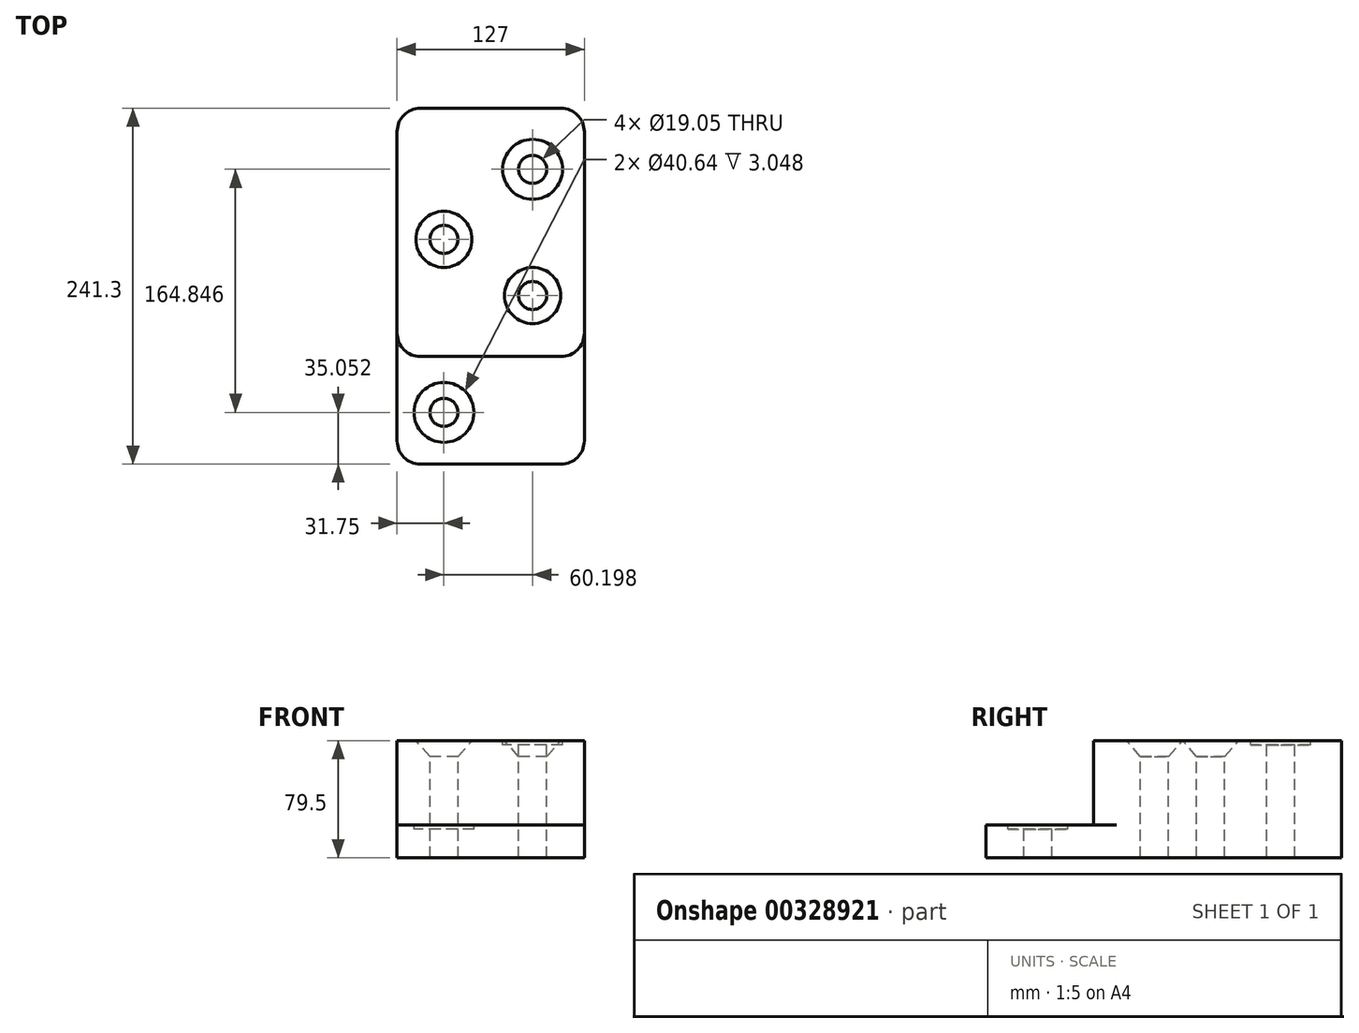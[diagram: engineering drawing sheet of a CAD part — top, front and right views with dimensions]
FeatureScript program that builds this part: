
annotation { "Feature Type Name" : "Feature", "Feature Type Description" : "" }
export const myFeature = defineFeature(function(context is Context, id is Id, definition is map)
    precondition{}
    {
        {
            var Q0;
            Q0=qCreatedBy(makeId("Top.planeOp"),FACE);
            var sketch = newSketch(context, id + "F0", { "sketchPlane" : qUnion([Q0])});
            skLineSegment(sketch, "E0.bottom", {"start": v(0, 0) * mm, "end": v(-127, 0) * mm});
            skLineSegment(sketch, "E0.top", {"start": v(0, -241.3) * mm, "end": v(-127, -241.3) * mm});
            skLineSegment(sketch, "E0.left", {"start": v(0, 0) * mm, "end": v(0, -241.3) * mm});
            skLineSegment(sketch, "E0.right", {"start": v(-127, 0) * mm, "end": v(-127, -241.3) * mm});
            skSolve(sketch);
        }
        {
            var Q0;
            Q0=makeQuery(id+"F0.imprint","IMPRINT",FACE,{"disambiguationData":[TD([[makeQuery(id+"F0.imprint","IMPRINT",EDGE,{"derivedFrom":sQuery(id+"F0.wireOp",EDGE,"E0.bottom")}),1.0]])]});
            extrude(context, id + "F1", {"entities" : qUnion([Q0]), "depth" : 22.35 * mm});
        }
        {
            var Q0;
            Q0=makeQuery(id+"F1.opExtrude","CAP_FACE",FACE,{"disambiguationData":[OSD([sQuery(id+"F0.wireOp",EDGE,"E0.bottom"),sQuery(id+"F0.wireOp",EDGE,"E0.top"),sQuery(id+"F0.wireOp",EDGE,"E0.left"),sQuery(id+"F0.wireOp",EDGE,"E0.right")])],"isStart":false});
            var sketch = newSketch(context, id + "F2", { "sketchPlane" : qUnion([Q0])});
            skLineSegment(sketch, "E1.bottom", {"start": v(-127, 0) * mm, "end": v(0, 0) * mm});
            skLineSegment(sketch, "E1.top", {"start": v(-127, -168.4) * mm, "end": v(0, -168.4) * mm});
            skLineSegment(sketch, "E1.left", {"start": v(-127, 0) * mm, "end": v(-127, -168.4) * mm});
            skLineSegment(sketch, "E1.right", {"start": v(0, 0) * mm, "end": v(0, -168.4) * mm});
            skSolve(sketch);
        }
        {
            var Q0;
            Q0=makeQuery(id+"F2.imprint","IMPRINT",FACE,{"disambiguationData":[TD([[makeQuery(id+"F2.imprint","IMPRINT",EDGE,{"derivedFrom":sQuery(id+"F2.wireOp",EDGE,"E1.bottom")}),1.0]])]});
            extrude(context, id + "F3", {"entities" : qUnion([Q0]), "operationType" : NewBodyOperationType.ADD, "depth" : 57.15 * mm});
        }
        {
            var Q0;
            Q0=makeQuery(id+"F3.opExtrude","SWEPT_EDGE",EDGE,{"disambiguationData":[OSD([sQuery(id+"F0.wireOp",EDGE,"E0.right"),sQuery(id+"F2.wireOp",EDGE,"E1.top"),sQuery(id+"F2.wireOp",EDGE,"E1.left")])]});
            var Q1;
            Q1=makeQuery(id+"F3.opExtrude","SWEPT_EDGE",EDGE,{"disambiguationData":[OSD([sQuery(id+"F0.wireOp",EDGE,"E0.left"),sQuery(id+"F2.wireOp",EDGE,"E1.top"),sQuery(id+"F2.wireOp",EDGE,"E1.right")])]});
            var Q2;
            Q2=makeQuery(id+"F3.boolean.opBoolean","MERGE",EDGE,{"derivedFrom":[makeQuery(id+"F1.opExtrude","SWEPT_EDGE",EDGE,{"disambiguationData":[OSD([sQuery(id+"F0.wireOp",EDGE,"E0.bottom"),sQuery(id+"F0.wireOp",EDGE,"E0.left")])]}),makeQuery(id+"F3.opExtrude","SWEPT_EDGE",EDGE,{"disambiguationData":[OSD([sQuery(id+"F2.wireOp",EDGE,"E1.bottom"),sQuery(id+"F2.wireOp",EDGE,"E1.right")])]})]});
            var Q3;
            Q3=makeQuery(id+"F3.boolean.opBoolean","MERGE",EDGE,{"derivedFrom":[makeQuery(id+"F1.opExtrude","SWEPT_EDGE",EDGE,{"disambiguationData":[OSD([sQuery(id+"F0.wireOp",EDGE,"E0.bottom"),sQuery(id+"F0.wireOp",EDGE,"E0.right")])]}),makeQuery(id+"F3.opExtrude","SWEPT_EDGE",EDGE,{"disambiguationData":[OSD([sQuery(id+"F2.wireOp",EDGE,"E1.bottom"),sQuery(id+"F2.wireOp",EDGE,"E1.left")])]})]});
            var Q4;
            Q4=makeQuery(id+"F1.opExtrude","SWEPT_EDGE",EDGE,{"disambiguationData":[OSD([sQuery(id+"F0.wireOp",EDGE,"E0.top"),sQuery(id+"F0.wireOp",EDGE,"E0.left")])]});
            var Q5;
            Q5=makeQuery(id+"F1.opExtrude","SWEPT_EDGE",EDGE,{"disambiguationData":[OSD([sQuery(id+"F0.wireOp",EDGE,"E0.top"),sQuery(id+"F0.wireOp",EDGE,"E0.right")])]});
            fillet(context, id + "F4", {"entities" : qUnion([Q0, Q1, Q2, Q3, Q4, Q5]), "radius" : 15.75 * mm, "tangentPropagation" : true, "allowEdgeOverflow" : false});
        }
        {
            var Q0;
            Q0=makeQuery(id+"F3.opExtrude","CAP_FACE",FACE,{"disambiguationData":[OSD([sQuery(id+"F2.wireOp",EDGE,"E1.bottom"),sQuery(id+"F2.wireOp",EDGE,"E1.top"),sQuery(id+"F2.wireOp",EDGE,"E1.left"),sQuery(id+"F2.wireOp",EDGE,"E1.right")])],"isStart":false});
            var sketch = newSketch(context, id + "F5", { "sketchPlane" : qUnion([Q0])});
            skCircle(sketch, "E2", {"center": v(-35.05, -41.4) * mm, "radius": 13.71 * mm});
            skCircle(sketch, "E3", {"center": v(-35.05, -127) * mm, "radius": 15.52 * mm});
            skCircle(sketch, "E4", {"center": v(-95.25, -88.9) * mm, "radius": 18.44 * mm});
            skCircle(sketch, "E5", {"center": v(-95.25, -206.25) * mm, "radius": 10.67 * mm});
            skSolve(sketch);
        }
        {
            var Q0;
            Q0=sQuery(id+"F5.wireOp",VERTEX,"E4.center");
            var Q1;
            Q1=sQuery(id+"F5.wireOp",VERTEX,"E3.center");
            var Q2;
            Q2=makeQuery(id+"F1.opExtrude","SWEPT_BODY",BODY,{"disambiguationData":[OSD([sQuery(id+"F0.wireOp",EDGE,"E0.bottom"),sQuery(id+"F0.wireOp",EDGE,"E0.top"),sQuery(id+"F0.wireOp",EDGE,"E0.left"),sQuery(id+"F0.wireOp",EDGE,"E0.right")])]});
            hole(context, id + "F6", {"style" : HoleStyle.C_SINK, "endStyle" : HoleEndStyle.THROUGH, "holeDiameter" : 19.05 * mm, "cSinkDiameter" : 38.1 * mm, "cSinkAngle" : 82 * degree, "tappedDepth" : 12.7 * mm, "tapClearance" : 3, "locations" : qUnion([Q0, Q1]), "scope" : qUnion([Q2])});
        }
        {
            var Q0;
            Q0=sQuery(id+"F5.wireOp",VERTEX,"E2.center");
            var Q1;
            Q1=makeQuery(id+"F1.opExtrude","SWEPT_BODY",BODY,{"disambiguationData":[OSD([sQuery(id+"F0.wireOp",EDGE,"E0.bottom"),sQuery(id+"F0.wireOp",EDGE,"E0.top"),sQuery(id+"F0.wireOp",EDGE,"E0.left"),sQuery(id+"F0.wireOp",EDGE,"E0.right")])]});
            hole(context, id + "F7", {"style" : HoleStyle.C_BORE, "endStyle" : HoleEndStyle.THROUGH, "holeDiameter" : 19.05 * mm, "cBoreDiameter" : 40.64 * mm, "cBoreDepth" : 3.05 * mm, "tappedDepth" : 12.7 * mm, "tapClearance" : 3, "locations" : qUnion([Q0]), "scope" : qUnion([Q1])});
        }
        {
            var Q0;
            Q0=sQuery(id+"F5.wireOp",VERTEX,"E5.center");
            var Q1;
            Q1=makeQuery(id+"F1.opExtrude","SWEPT_BODY",BODY,{"disambiguationData":[OSD([sQuery(id+"F0.wireOp",EDGE,"E0.bottom"),sQuery(id+"F0.wireOp",EDGE,"E0.top"),sQuery(id+"F0.wireOp",EDGE,"E0.left"),sQuery(id+"F0.wireOp",EDGE,"E0.right")])]});
            hole(context, id + "F8", {"style" : HoleStyle.C_BORE, "endStyle" : HoleEndStyle.THROUGH, "holeDiameter" : 19.05 * mm, "cBoreDiameter" : 40.64 * mm, "cBoreDepth" : 3.05 * mm, "tappedDepth" : 12.7 * mm, "tapClearance" : 3, "locations" : qUnion([Q0]), "scope" : qUnion([Q1])});
        }
    });
